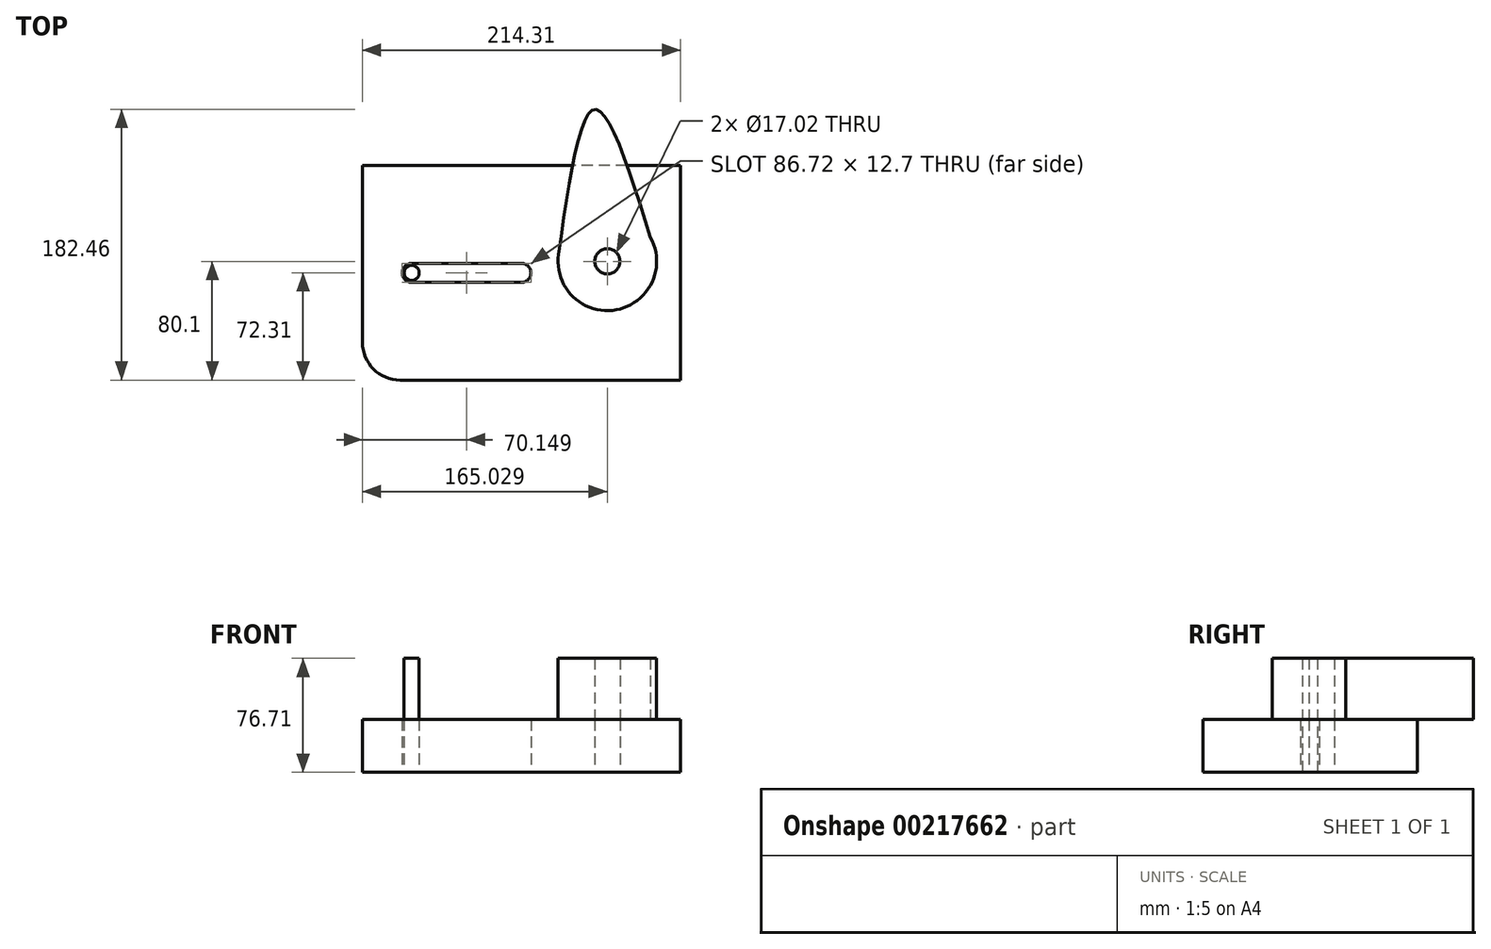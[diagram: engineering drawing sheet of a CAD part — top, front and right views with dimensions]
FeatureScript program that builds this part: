
annotation { "Feature Type Name" : "Feature", "Feature Type Description" : "" }
export const myFeature = defineFeature(function(context is Context, id is Id, definition is map)
    precondition{}
    {
        {
            var Q0;
            Q0=qCreatedBy(makeId("Top.planeOp"),FACE);
            var sketch = newSketch(context, id + "F0", { "sketchPlane" : qUnion([Q0])});
            skLineSegment(sketch, "E0.bottom", {"start": v(-35.32, -26.12) * mm, "end": v(-249.63, -26.12) * mm});
            skLineSegment(sketch, "E0.top", {"start": v(-35.32, 118.5) * mm, "end": v(-249.63, 118.5) * mm});
            skLineSegment(sketch, "E0.left", {"start": v(-35.32, -26.12) * mm, "end": v(-35.32, 118.5) * mm});
            skLineSegment(sketch, "E0.right", {"start": v(-249.63, -26.12) * mm, "end": v(-249.63, 118.5) * mm});
            skPoint(sketch, "E0.middle", {"position": v(-142.47, 46.2) * mm});
            skCircle(sketch, "E1", {"center": v(-84.6, 53.98) * mm, "radius": 8.5 * mm});
            skLineSegment(sketch, "E2", {"start": v(-216.49, 46.2) * mm, "end": v(-142.47, 46.2) * mm});
            skArc(sketch, "E3.0.startCap", {"start": v(-216.49, 39.84) * mm, "mid": v(-222.84, 46.2) * mm, "end": v(-216.49, 52.54) * mm});
            skArc(sketch, "E3.0.endCap", {"start": v(-142.47, 52.54) * mm, "mid": v(-136.12, 46.2) * mm, "end": v(-142.47, 39.84) * mm});
            skLineSegment(sketch, "E3.0.left", {"start": v(-216.49, 52.54) * mm, "end": v(-142.47, 52.54) * mm});
            skLineSegment(sketch, "E3.0.right", {"start": v(-216.49, 39.84) * mm, "end": v(-142.47, 39.84) * mm});
            skSolve(sketch);
        }
        {
            var Q0;
            Q0=makeQuery(id+"F0.imprint","IMPRINT",FACE,{"disambiguationData":[TD([[makeQuery(id+"F0.imprint","IMPRINT",EDGE,{"derivedFrom":sQuery(id+"F0.wireOp",EDGE,"E0.bottom")}),-1.0]])]});
            extrude(context, id + "F1", {"entities" : qUnion([Q0]), "depth" : 35.56 * mm});
        }
        {
            var Q0;
            Q0=makeQuery(id+"F1.opExtrude","CAP_FACE",FACE,{"disambiguationData":[OSD([sQuery(id+"F0.wireOp",EDGE,"E0.bottom"),sQuery(id+"F0.wireOp",EDGE,"E0.top"),sQuery(id+"F0.wireOp",EDGE,"E0.left"),sQuery(id+"F0.wireOp",EDGE,"E0.right"),sQuery(id+"F0.wireOp",EDGE,"E1"),sQuery(id+"F0.wireOp",EDGE,"E3.0.startCap"),sQuery(id+"F0.wireOp",EDGE,"E3.0.endCap"),sQuery(id+"F0.wireOp",EDGE,"E3.0.left"),sQuery(id+"F0.wireOp",EDGE,"E3.0.right")])],"isStart":false});
            var sketch = newSketch(context, id + "F2", { "sketchPlane" : qUnion([Q0])});
            skCircle(sketch, "E4", {"center": v(-84.6, 53.98) * mm, "radius": 33.23 * mm});
            skFitSpline(sketch, "E5", {"points": [v(-117.5, 58.7) * mm, v(-93.1, 156.33) * mm, v(-55.52, 70.05) * mm], "startDerivative": vector(40.94, 285.4) * mm, "endDerivative": vector(83.34, -265.88) * mm});
            skSolve(sketch);
        }
        {
            var Q0;
            Q0=makeQuery(id+"F2.imprint","IMPRINT",FACE,{"disambiguationData":[TD([[makeQuery(id+"F2.imprint","IMPRINT",EDGE,{"derivedFrom":makeQuery(id+"F1.opExtrude","CAP_EDGE",EDGE,{"disambiguationData":[OSD([sQuery(id+"F0.wireOp",EDGE,"E0.bottom")])],"isStart":false})}),-1.0]])]});
            var sketch = newSketch(context, id + "F3", { "sketchPlane" : qUnion([Q0])});
            skCircle(sketch, "E6", {"center": v(-216.49, 46.2) * mm, "radius": 5.08 * mm});
            skSolve(sketch);
        }
        {
            var Q0;
            Q0 = qSketchRegion(id + "F3", true);
            var Q1;
            Q1=makeQuery(id+"F1.opExtrude","CAP_FACE",FACE,{"disambiguationData":[OSD([sQuery(id+"F0.wireOp",EDGE,"E0.bottom"),sQuery(id+"F0.wireOp",EDGE,"E0.top"),sQuery(id+"F0.wireOp",EDGE,"E0.left"),sQuery(id+"F0.wireOp",EDGE,"E0.right"),sQuery(id+"F0.wireOp",EDGE,"E1"),sQuery(id+"F0.wireOp",EDGE,"E3.0.startCap"),sQuery(id+"F0.wireOp",EDGE,"E3.0.endCap"),sQuery(id+"F0.wireOp",EDGE,"E3.0.left"),sQuery(id+"F0.wireOp",EDGE,"E3.0.right")])],"isStart":true});
            extrude(context, id + "F4", {"entities" : qUnion([Q0]), "depth" : 41.15 * mm, "hasSecondDirection" : true, "secondDirectionBound" : SecondDirectionBoundingType.UP_TO_SURFACE, "secondDirectionOppositeDirection" : true, "secondDirectionBoundEntityFace" : qUnion([Q1]), "secondDirectionDepth" : 25.4 * mm});
        }
        {
            var Q0;
            Q0=makeQuery(id+"F2.imprint","IMPRINT",FACE,{"disambiguationData":[TD([[makeQuery(id+"F2.imprint","IMPRINT",EDGE,{"derivedFrom":makeQuery(id+"F1.opExtrude","CAP_EDGE",EDGE,{"disambiguationData":[OSD([sQuery(id+"F0.wireOp",EDGE,"E1")])],"isStart":false})}),-1.0]])]});
            var Q1;
            {var subQ0=sQuery(id+"F2.wireOp",EDGE,"E5");var subQ1=sQuery(id+"F2.wireOp",EDGE,"E4");var subQ2=makeQuery(id+"F2.imprint","INTERSECT",VERTEX,{"disambiguationData":[OD(0.0)],"derivedFrom":[subQ1,subQ0]});Q1=makeQuery(id+"F2.imprint","IMPRINT",FACE,{"disambiguationData":[TD([[makeQuery(id+"F2.imprint","IMPRINT",EDGE,{"disambiguationData":[TD([[subQ2,1.0]])],"derivedFrom":subQ1}),-1.0]])]});}
            var Q2;
            {var subQ0=sQuery(id+"F2.wireOp",EDGE,"E5");var subQ1=makeQuery(id+"F1.opExtrude","CAP_EDGE",EDGE,{"disambiguationData":[OSD([sQuery(id+"F0.wireOp",EDGE,"E0.top")])],"isStart":false});var subQ2=makeQuery(id+"F2.imprint","INTERSECT",VERTEX,{"disambiguationData":[OD(0.0)],"derivedFrom":[subQ1,subQ0]});Q2=makeQuery(id+"F2.imprint","IMPRINT",FACE,{"disambiguationData":[TD([[makeQuery(id+"F2.imprint","IMPRINT",EDGE,{"disambiguationData":[TD([[subQ2,-1.0]])],"derivedFrom":subQ0}),-1.0]])]});}
            var Q3;
            Q3=makeQuery(id+"F4.opExtrude","CAP_FACE",FACE,{"disambiguationData":[OSD([sQuery(id+"F3.wireOp",EDGE,"E6")])],"isStart":false});
            extrude(context, id + "F5", {"entities" : qUnion([Q0, Q1, Q2]), "endBound" : BoundingType.UP_TO_SURFACE, "endBoundEntityFace" : qUnion([Q3]), "depth" : 25.4 * mm});
        }
        {
            var Q0;
            Q0=makeQuery(id+"F1.opExtrude","SWEPT_EDGE",EDGE,{"disambiguationData":[OSD([sQuery(id+"F0.wireOp",EDGE,"E0.bottom"),sQuery(id+"F0.wireOp",EDGE,"E0.right")])]});
            fillet(context, id + "F6", {"entities" : qUnion([Q0]), "radius" : 25.4 * mm, "tangentPropagation" : true, "allowEdgeOverflow" : false});
        }
    });
